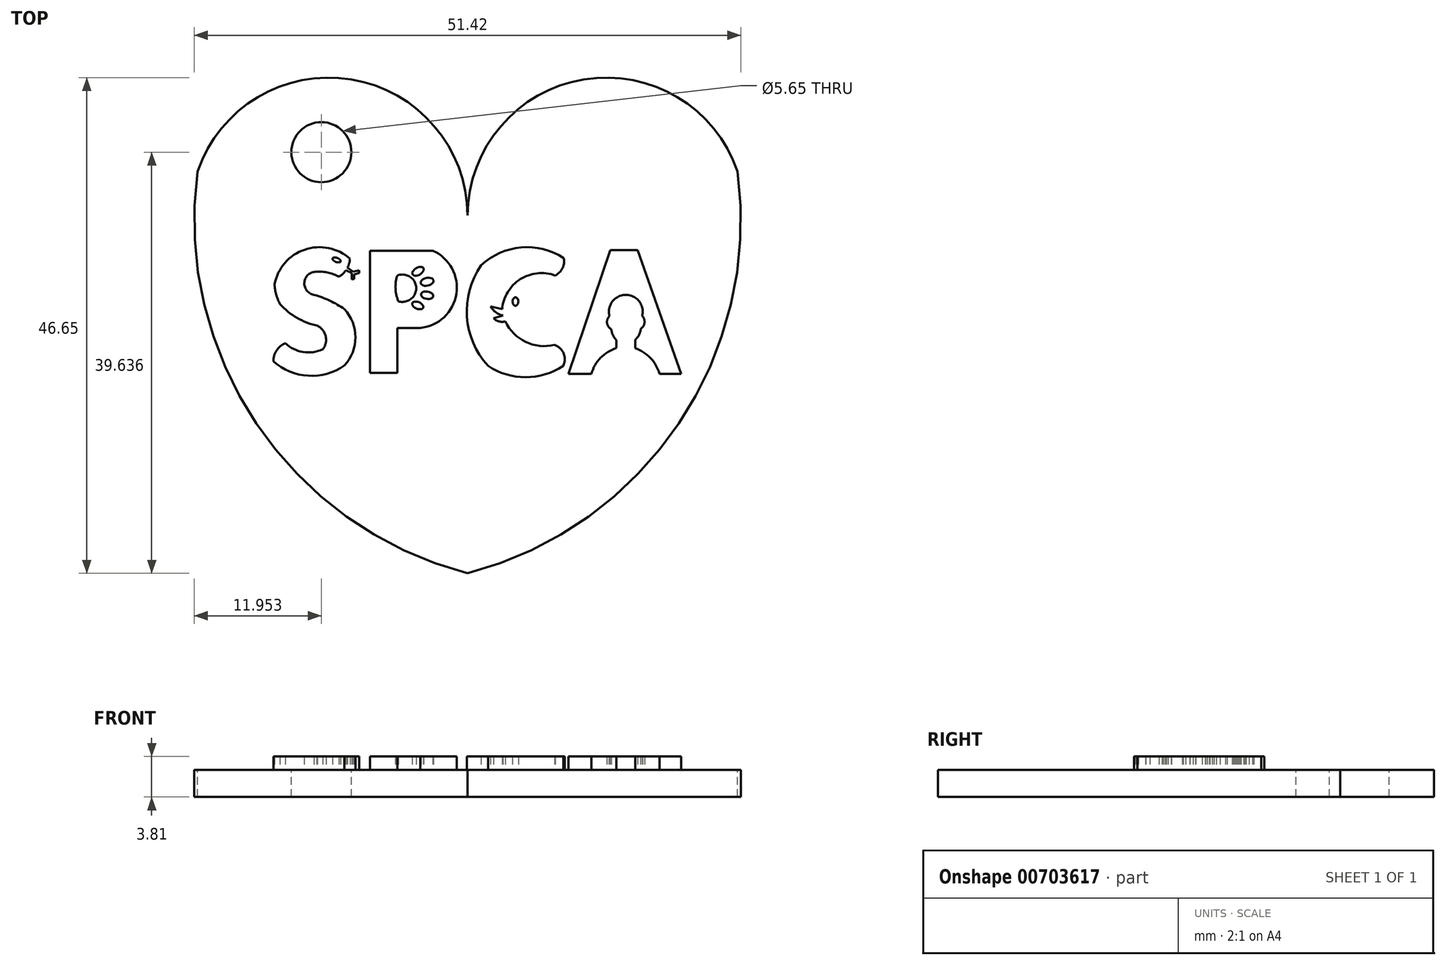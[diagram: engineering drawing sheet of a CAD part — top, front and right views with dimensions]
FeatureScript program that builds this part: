
annotation { "Feature Type Name" : "Feature", "Feature Type Description" : "" }
export const myFeature = defineFeature(function(context is Context, id is Id, definition is map)
    precondition{}
    {
        {
            var Q0;
            Q0=qCreatedBy(makeId("Top.planeOp"),FACE);
            var sketch = newSketch(context, id + "F0", { "sketchPlane" : qUnion([Q0])});
            skArc(sketch, "E0", {"start": v(25.4, 37.83) * mm, "mid": v(10.95, 46.48) * mm, "end": v(0, 33.68) * mm});
            skArc(sketch, "E1", {"start": v(0, 0) * mm, "mid": v(19.87, 14.1) * mm, "end": v(25.4, 37.83) * mm});
            skArc(sketch, "E2.MirrorCS", {"start": v(-25.4, 37.83) * mm, "mid": v(-10.95, 46.48) * mm, "end": v(0, 33.68) * mm});
            skArc(sketch, "E3.MirrorCS", {"start": v(0, 0) * mm, "mid": v(-19.87, 14.1) * mm, "end": v(-25.4, 37.83) * mm});
            skSolve(sketch);
        }
        {
            var Q0;
            Q0=makeQuery(id+"F0.imprint","IMPRINT",FACE,{"disambiguationData":[TD([[makeQuery(id+"F0.imprint","IMPRINT",EDGE,{"derivedFrom":sQuery(id+"F0.wireOp",EDGE,"E0")}),1.0]])]});
            var sketch = newSketch(context, id + "F1", { "sketchPlane" : qUnion([Q0])});
            skCircle(sketch, "E4", {"center": v(-13.76, 39.64) * mm, "radius": 2.82 * mm});
            skPoint(sketch, "E4.first.point", {"position": v(-16.32, 40.83) * mm});
            skPoint(sketch, "E4.second.point", {"position": v(-11.9, 37.52) * mm});
            skPoint(sketch, "E4.third.point", {"position": v(-11.9, 41.76) * mm});
            skSolve(sketch);
        }
        {
            var Q0;
            Q0=makeQuery(id+"F1.imprint","IMPRINT",FACE,{"disambiguationData":[TD([[makeQuery(id+"F1.imprint","IMPRINT",EDGE,{"derivedFrom":sQuery(id+"F1.wireOp",EDGE,"E4")}),-1.0]])]});
            extrude(context, id + "F2", {"entities" : qUnion([Q0]), "oppositeDirection" : true, "depth" : 2.54 * mm, "offsetDistance" : 25.4 * mm});
        }
        {
            var Q0;
            Q0=makeQuery(id+"F0.imprint","IMPRINT",FACE,{"disambiguationData":[TD([[makeQuery(id+"F0.imprint","IMPRINT",EDGE,{"derivedFrom":sQuery(id+"F0.wireOp",EDGE,"E0")}),1.0]])]});
            var sketch = newSketch(context, id + "F3", { "sketchPlane" : qUnion([Q0])});
            skArc(sketch, "E5", {"start": v(-11.06, 29.6) * mm, "mid": v(-15.31, 30.47) * mm, "end": v(-18.16, 27.2) * mm});
            skArc(sketch, "E6", {"start": v(-17.64, 25.33) * mm, "mid": v(-16.05, 24.04) * mm, "end": v(-14.13, 23.3) * mm});
            skArc(sketch, "E7", {"start": v(-18.16, 27.2) * mm, "mid": v(-18, 26.23) * mm, "end": v(-17.64, 25.33) * mm});
            skArc(sketch, "E8", {"start": v(-17.15, 21.66) * mm, "mid": v(-15.47, 20.82) * mm, "end": v(-13.61, 21.08) * mm});
            skArc(sketch, "E9", {"start": v(-13.61, 21.08) * mm, "mid": v(-13.35, 22.31) * mm, "end": v(-14.13, 23.3) * mm});
            skArc(sketch, "E10", {"start": v(-17.15, 21.66) * mm, "mid": v(-17.97, 20.96) * mm, "end": v(-18.27, 19.93) * mm});
            skArc(sketch, "E11", {"start": v(-18.27, 19.93) * mm, "mid": v(-15, 18.6) * mm, "end": v(-11.58, 19.55) * mm});
            skArc(sketch, "E12", {"start": v(-11.58, 19.55) * mm, "mid": v(-10.55, 22.2) * mm, "end": v(-11.58, 24.86) * mm});
            skArc(sketch, "E13", {"start": v(-11.58, 24.86) * mm, "mid": v(-12.95, 25.65) * mm, "end": v(-14.43, 26.2) * mm});
            skArc(sketch, "E14", {"start": v(-14.19, 28.37) * mm, "mid": v(-15.35, 27.4) * mm, "end": v(-14.43, 26.2) * mm});
            skArc(sketch, "E15", {"start": v(-12.1, 27.9) * mm, "mid": v(-13.11, 28.3) * mm, "end": v(-14.19, 28.37) * mm});
            skArc(sketch, "E16", {"start": v(-12.1, 27.9) * mm, "mid": v(-11.74, 28.18) * mm, "end": v(-11.44, 28.52) * mm});
            skLineSegment(sketch, "E17", {"start": v(-11.3, 28.78) * mm, "end": v(-10.75, 28.4) * mm});
            skLineSegment(sketch, "E18", {"start": v(-10.75, 28.4) * mm, "end": v(-10.19, 28.5) * mm});
            skLineSegment(sketch, "E19", {"start": v(-10.19, 28.5) * mm, "end": v(-10.19, 28.25) * mm});
            skLineSegment(sketch, "E20", {"start": v(-10.19, 28.25) * mm, "end": v(-10.68, 28.14) * mm});
            skLineSegment(sketch, "E21", {"start": v(-10.68, 28.14) * mm, "end": v(-10.68, 27.67) * mm});
            skLineSegment(sketch, "E22", {"start": v(-10.68, 27.67) * mm, "end": v(-10.9, 27.67) * mm});
            skLineSegment(sketch, "E23", {"start": v(-10.9, 27.67) * mm, "end": v(-10.9, 28.25) * mm});
            skLineSegment(sketch, "E24", {"start": v(-10.9, 28.25) * mm, "end": v(-11.44, 28.52) * mm});
            skEllipse(sketch, "E25", {"center": v(-12.33, 29.5) * mm, "majorRadius": 0.4 * mm, "minorRadius": 0.2 * mm, "majorAxis": v(0.94, -0.35)});
            skArc(sketch, "E26.trimOffspring", {"start": v(-11.3, 28.78) * mm, "mid": v(-11.13, 29.18) * mm, "end": v(-11.06, 29.6) * mm});
            skSolve(sketch);
        }
        {
            var Q0;
            Q0 = qSketchRegion(id + "F3", true);
            extrude(context, id + "F4", {"entities" : qUnion([Q0]), "operationType" : NewBodyOperationType.ADD, "depth" : 1.27 * mm, "offsetDistance" : 25.4 * mm});
        }
        {
            var Q0;
            Q0=makeQuery(id+"F0.imprint","IMPRINT",FACE,{"disambiguationData":[TD([[makeQuery(id+"F0.imprint","IMPRINT",EDGE,{"derivedFrom":sQuery(id+"F0.wireOp",EDGE,"E0")}),1.0]])]});
            var sketch = newSketch(context, id + "F5", { "sketchPlane" : qUnion([Q0])});
            skLineSegment(sketch, "E27", {"start": v(-9.17, 30.37) * mm, "end": v(-9.17, 18.86) * mm});
            skLineSegment(sketch, "E28", {"start": v(-9.17, 18.86) * mm, "end": v(-6.62, 18.86) * mm});
            skLineSegment(sketch, "E29", {"start": v(-6.62, 18.86) * mm, "end": v(-6.62, 23.08) * mm});
            skLineSegment(sketch, "E30", {"start": v(-6.62, 23.08) * mm, "end": v(-4.43, 23.08) * mm});
            skLineSegment(sketch, "E31", {"start": v(-9.17, 30.37) * mm, "end": v(-3.26, 30.37) * mm});
            skArc(sketch, "E32", {"start": v(-4.43, 23.08) * mm, "mid": v(-1.06, 26.28) * mm, "end": v(-3.26, 30.37) * mm});
            skArc(sketch, "E33", {"start": v(-6.62, 28.02) * mm, "mid": v(-6.78, 26.8) * mm, "end": v(-6.51, 25.6) * mm});
            skArc(sketch, "E34", {"start": v(-6.51, 25.6) * mm, "mid": v(-4.83, 26.88) * mm, "end": v(-6.62, 28.02) * mm});
            skEllipse(sketch, "E35", {"center": v(-4.66, 28.42) * mm, "majorRadius": 0.6 * mm, "minorRadius": 0.34 * mm, "majorAxis": v(0.86, 0.5)});
            skEllipse(sketch, "E36", {"center": v(-3.8, 27.44) * mm, "majorRadius": 0.61 * mm, "minorRadius": 0.36 * mm, "majorAxis": v(0.97, 0.23)});
            skEllipse(sketch, "E37", {"center": v(-3.8, 26.17) * mm, "majorRadius": 0.58 * mm, "minorRadius": 0.35 * mm, "majorAxis": v(0.98, -0.18)});
            skEllipse(sketch, "E38", {"center": v(-4.68, 25.2) * mm, "majorRadius": 0.55 * mm, "minorRadius": 0.32 * mm, "majorAxis": v(0.92, -0.39)});
            skSolve(sketch);
        }
        {
            var Q0;
            Q0 = qSketchRegion(id + "F5", true);
            extrude(context, id + "F6", {"entities" : qUnion([Q0]), "operationType" : NewBodyOperationType.ADD, "depth" : 1.27 * mm, "offsetDistance" : 25.4 * mm});
        }
        {
            var Q0;
            Q0=makeQuery(id+"F0.imprint","IMPRINT",FACE,{"disambiguationData":[TD([[makeQuery(id+"F0.imprint","IMPRINT",EDGE,{"derivedFrom":sQuery(id+"F0.wireOp",EDGE,"E0")}),1.0]])]});
            var sketch = newSketch(context, id + "F7", { "sketchPlane" : qUnion([Q0])});
            skArc(sketch, "E39", {"start": v(9.06, 29.66) * mm, "mid": v(5.05, 30.67) * mm, "end": v(1.27, 28.98) * mm});
            skArc(sketch, "E40", {"start": v(1.27, 28.98) * mm, "mid": v(-0.06, 24.14) * mm, "end": v(1.92, 19.53) * mm});
            skArc(sketch, "E41", {"start": v(1.92, 19.53) * mm, "mid": v(5.46, 18.45) * mm, "end": v(9, 19.53) * mm});
            skArc(sketch, "E42", {"start": v(9, 19.53) * mm, "mid": v(9.04, 20.7) * mm, "end": v(8.17, 21.5) * mm});
            skArc(sketch, "E43", {"start": v(8.24, 28.02) * mm, "mid": v(4.96, 27.67) * mm, "end": v(3.26, 24.85) * mm});
            skArc(sketch, "E44", {"start": v(3.55, 23.7) * mm, "mid": v(5.47, 21.78) * mm, "end": v(8.17, 21.5) * mm});
            skArc(sketch, "E45", {"start": v(8.24, 28.02) * mm, "mid": v(8.92, 28.7) * mm, "end": v(9.06, 29.66) * mm});
            skEllipse(sketch, "E46", {"center": v(4.5, 25.58) * mm, "majorRadius": 0.4 * mm, "minorRadius": 0.27 * mm, "majorAxis": v(0, -1)});
            skLineSegment(sketch, "E47", {"start": v(3.26, 24.85) * mm, "end": v(2.16, 25.13) * mm});
            skLineSegment(sketch, "E48", {"start": v(3.34, 24.25) * mm, "end": v(2.44, 24.01) * mm});
            skArc(sketch, "E49", {"start": v(2.16, 25.13) * mm, "mid": v(2.66, 24.57) * mm, "end": v(3.34, 24.25) * mm});
            skArc(sketch, "E50", {"start": v(2.44, 24.01) * mm, "mid": v(2.95, 23.7) * mm, "end": v(3.55, 23.7) * mm});
            skSolve(sketch);
        }
        {
            var Q0;
            Q0 = qSketchRegion(id + "F7", true);
            extrude(context, id + "F8", {"entities" : qUnion([Q0]), "operationType" : NewBodyOperationType.ADD, "depth" : 1.27 * mm, "offsetDistance" : 25.4 * mm});
        }
        {
            var Q0;
            Q0=makeQuery(id+"F0.imprint","IMPRINT",FACE,{"disambiguationData":[TD([[makeQuery(id+"F0.imprint","IMPRINT",EDGE,{"derivedFrom":sQuery(id+"F0.wireOp",EDGE,"E0")}),1.0]])]});
            var sketch = newSketch(context, id + "F9", { "sketchPlane" : qUnion([Q0])});
            skLineSegment(sketch, "E51", {"start": v(13.42, 30.42) * mm, "end": v(16.01, 30.42) * mm});
            skLineSegment(sketch, "E52", {"start": v(16.01, 30.42) * mm, "end": v(20.08, 18.77) * mm});
            skLineSegment(sketch, "E53", {"start": v(20.08, 18.77) * mm, "end": v(18.07, 18.77) * mm});
            skLineSegment(sketch, "E54", {"start": v(9.49, 18.77) * mm, "end": v(13.42, 30.42) * mm});
            skArc(sketch, "E55", {"start": v(16.43, 24.22) * mm, "mid": v(14.89, 26.2) * mm, "end": v(13.36, 24.21) * mm});
            skArc(sketch, "E56", {"start": v(14, 21.2) * mm, "mid": v(12.52, 20.28) * mm, "end": v(11.65, 18.77) * mm});
            skArc(sketch, "E57", {"start": v(18.07, 18.77) * mm, "mid": v(17.2, 20.26) * mm, "end": v(15.76, 21.19) * mm});
            skLineSegment(sketch, "E58.trimOffspring", {"start": v(11.65, 18.77) * mm, "end": v(9.49, 18.77) * mm});
            skArc(sketch, "E59", {"start": v(13.36, 24.21) * mm, "mid": v(13.13, 23.55) * mm, "end": v(13.52, 22.98) * mm});
            skArc(sketch, "E60", {"start": v(16.3, 23) * mm, "mid": v(16.65, 23.58) * mm, "end": v(16.43, 24.22) * mm});
            skArc(sketch, "E61", {"start": v(13.52, 22.98) * mm, "mid": v(13.67, 22.42) * mm, "end": v(14, 21.95) * mm});
            skArc(sketch, "E62", {"start": v(15.76, 21.96) * mm, "mid": v(16.13, 22.43) * mm, "end": v(16.3, 23) * mm});
            skLineSegment(sketch, "E63", {"start": v(14, 21.95) * mm, "end": v(14, 21.2) * mm});
            skLineSegment(sketch, "E64", {"start": v(15.76, 21.96) * mm, "end": v(15.76, 21.19) * mm});
            skSolve(sketch);
        }
        {
            var Q0;
            Q0 = qSketchRegion(id + "F9", true);
            extrude(context, id + "F10", {"entities" : qUnion([Q0]), "operationType" : NewBodyOperationType.ADD, "depth" : 1.27 * mm, "offsetDistance" : 25.4 * mm});
        }
    });
